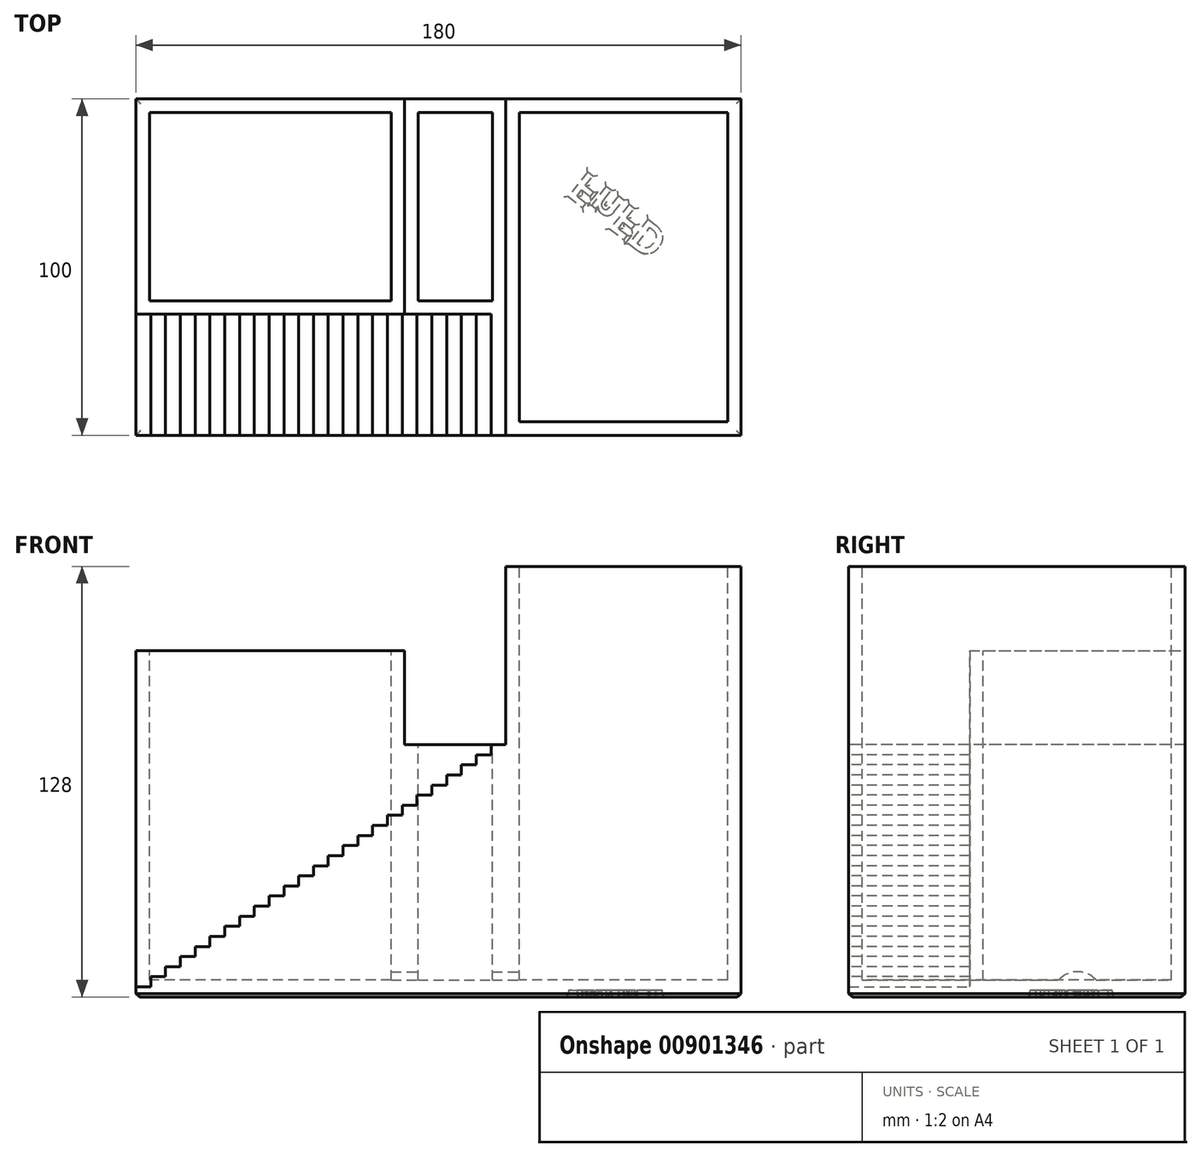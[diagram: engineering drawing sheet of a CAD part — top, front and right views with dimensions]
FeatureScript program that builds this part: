
annotation { "Feature Type Name" : "Feature", "Feature Type Description" : "" }
export const myFeature = defineFeature(function(context is Context, id is Id, definition is map)
    precondition{}
    {
        {
            var Q0;
            Q0=qCreatedBy(makeId("Top.planeOp"),FACE);
            var sketch = newSketch(context, id + "F0", { "sketchPlane" : qUnion([Q0])});
            skLineSegment(sketch, "E0.bottom", {"start": v(-90, -50) * mm, "end": v(90, -50) * mm});
            skLineSegment(sketch, "E0.top", {"start": v(-90, 50) * mm, "end": v(90, 50) * mm});
            skLineSegment(sketch, "E0.left", {"start": v(-90, -50) * mm, "end": v(-90, 50) * mm});
            skLineSegment(sketch, "E0.right", {"start": v(90, -50) * mm, "end": v(90, 50) * mm});
            skPoint(sketch, "E0.middle", {"position": v(0, 0) * mm});
            skSolve(sketch);
        }
        {
            var Q0;
            Q0=makeQuery(id+"F0.imprint","IMPRINT",FACE,{"disambiguationData":[TD([[makeQuery(id+"F0.imprint","IMPRINT",EDGE,{"derivedFrom":sQuery(id+"F0.wireOp",EDGE,"E0.bottom")}),1.0]])]});
            extrude(context, id + "F1", {"entities" : qUnion([Q0]), "depth" : 128 * mm, "offsetDistance" : 25 * mm});
        }
        {
            var Q0;
            Q0=makeQuery(id+"F1.opExtrude","SWEPT_FACE",FACE,{"disambiguationData":[OSD([sQuery(id+"F0.wireOp",EDGE,"E0.bottom")])]});
            var sketch = newSketch(context, id + "F2", { "sketchPlane" : qUnion([Q0])});
            skLineSegment(sketch, "E1.bottom", {"start": v(-90, 128) * mm, "end": v(20, 128) * mm});
            skLineSegment(sketch, "E1.top", {"start": v(-90, 75) * mm, "end": v(20, 75) * mm});
            skLineSegment(sketch, "E1.left", {"start": v(-90, 128) * mm, "end": v(-90, 75) * mm});
            skLineSegment(sketch, "E1.right", {"start": v(20, 128) * mm, "end": v(20, 75) * mm});
            skLineSegment(sketch, "E2", {"start": v(-90, 0) * mm, "end": v(20, 75) * mm, "construction": true});
            skLineSegment(sketch, "E3", {"start": v(-90, 0) * mm, "end": v(-90, 3) * mm});
            skLineSegment(sketch, "E4", {"start": v(-90, 3) * mm, "end": v(-85.6, 3) * mm});
            skLineSegment(sketch, "E5", {"start": v(-85.6, 3) * mm, "end": v(-85.6, 6) * mm});
            skLineSegment(sketch, "E6", {"start": v(-85.6, 6) * mm, "end": v(-81.2, 6) * mm});
            skLineSegment(sketch, "E7", {"start": v(-81.2, 6) * mm, "end": v(-81.2, 9) * mm});
            skLineSegment(sketch, "E8", {"start": v(-81.2, 9) * mm, "end": v(-76.8, 9) * mm});
            skLineSegment(sketch, "E9", {"start": v(-76.8, 9) * mm, "end": v(-76.8, 12) * mm});
            skLineSegment(sketch, "E10", {"start": v(-76.8, 12) * mm, "end": v(-72.4, 12) * mm});
            skLineSegment(sketch, "E11", {"start": v(-72.4, 12) * mm, "end": v(-72.4, 15) * mm});
            skLineSegment(sketch, "E12", {"start": v(-72.4, 15) * mm, "end": v(-68, 15) * mm});
            skLineSegment(sketch, "E13", {"start": v(-68, 15) * mm, "end": v(-68, 18) * mm});
            skLineSegment(sketch, "E14", {"start": v(-68, 18) * mm, "end": v(-63.6, 18) * mm});
            skLineSegment(sketch, "E15", {"start": v(-63.6, 18) * mm, "end": v(-63.6, 21) * mm});
            skLineSegment(sketch, "E16", {"start": v(-63.6, 21) * mm, "end": v(-59.2, 21) * mm});
            skLineSegment(sketch, "E17", {"start": v(-59.2, 21) * mm, "end": v(-59.2, 24) * mm});
            skLineSegment(sketch, "E18", {"start": v(-59.2, 24) * mm, "end": v(-54.8, 24) * mm});
            skLineSegment(sketch, "E19", {"start": v(-54.8, 24) * mm, "end": v(-54.8, 27) * mm});
            skLineSegment(sketch, "E20", {"start": v(-54.8, 27) * mm, "end": v(-50.4, 27) * mm});
            skLineSegment(sketch, "E21", {"start": v(-50.4, 27) * mm, "end": v(-50.4, 30) * mm});
            skLineSegment(sketch, "E22", {"start": v(-50.4, 30) * mm, "end": v(-46, 30) * mm});
            skLineSegment(sketch, "E23", {"start": v(-46, 30) * mm, "end": v(-46, 33) * mm});
            skLineSegment(sketch, "E24", {"start": v(-46, 33) * mm, "end": v(-41.6, 33) * mm});
            skLineSegment(sketch, "E25", {"start": v(-41.6, 33) * mm, "end": v(-41.6, 36) * mm});
            skLineSegment(sketch, "E26", {"start": v(-41.6, 36) * mm, "end": v(-37.2, 36) * mm});
            skLineSegment(sketch, "E27", {"start": v(-37.2, 36) * mm, "end": v(-37.2, 39) * mm});
            skLineSegment(sketch, "E28", {"start": v(-37.2, 39) * mm, "end": v(-32.8, 39) * mm});
            skLineSegment(sketch, "E29", {"start": v(-32.8, 39) * mm, "end": v(-32.8, 42) * mm});
            skLineSegment(sketch, "E30", {"start": v(-32.8, 42) * mm, "end": v(-28.4, 42) * mm});
            skLineSegment(sketch, "E31", {"start": v(-28.4, 42) * mm, "end": v(-28.4, 45) * mm});
            skLineSegment(sketch, "E32", {"start": v(-28.4, 45) * mm, "end": v(-24, 45) * mm});
            skLineSegment(sketch, "E33", {"start": v(-24, 45) * mm, "end": v(-24, 48) * mm});
            skLineSegment(sketch, "E34", {"start": v(-24, 48) * mm, "end": v(-19.6, 48) * mm});
            skLineSegment(sketch, "E35", {"start": v(-19.6, 48) * mm, "end": v(-19.6, 51) * mm});
            skLineSegment(sketch, "E36", {"start": v(-19.6, 51) * mm, "end": v(-15.2, 51) * mm});
            skLineSegment(sketch, "E37", {"start": v(-15.2, 51) * mm, "end": v(-15.2, 54) * mm});
            skLineSegment(sketch, "E38", {"start": v(-15.2, 54) * mm, "end": v(-10.8, 54) * mm});
            skLineSegment(sketch, "E39", {"start": v(-10.8, 54) * mm, "end": v(-10.8, 57) * mm});
            skLineSegment(sketch, "E40", {"start": v(-10.8, 57) * mm, "end": v(-6.4, 57) * mm});
            skLineSegment(sketch, "E41", {"start": v(-6.4, 57) * mm, "end": v(-6.4, 60) * mm});
            skLineSegment(sketch, "E42", {"start": v(-6.4, 60) * mm, "end": v(-2, 60) * mm});
            skLineSegment(sketch, "E43", {"start": v(-2, 60) * mm, "end": v(-2, 63) * mm});
            skLineSegment(sketch, "E44", {"start": v(-2, 63) * mm, "end": v(2.4, 63) * mm});
            skLineSegment(sketch, "E45", {"start": v(2.4, 63) * mm, "end": v(2.4, 63) * mm});
            skLineSegment(sketch, "E46", {"start": v(2.4, 63) * mm, "end": v(2.4, 66) * mm});
            skLineSegment(sketch, "E47", {"start": v(2.4, 66) * mm, "end": v(6.8, 66) * mm});
            skLineSegment(sketch, "E48", {"start": v(6.8, 66) * mm, "end": v(6.8, 69) * mm});
            skLineSegment(sketch, "E49", {"start": v(6.8, 69) * mm, "end": v(11.2, 69) * mm});
            skLineSegment(sketch, "E50", {"start": v(11.2, 69) * mm, "end": v(11.2, 72) * mm});
            skLineSegment(sketch, "E51", {"start": v(11.2, 72) * mm, "end": v(15.6, 72) * mm});
            skLineSegment(sketch, "E52", {"start": v(15.6, 72) * mm, "end": v(15.6, 75) * mm});
            skLineSegment(sketch, "E53", {"start": v(15.6, 75) * mm, "end": v(20, 75) * mm});
            skLineSegment(sketch, "E54", {"start": v(20, 75) * mm, "end": v(20, 78) * mm});
            skLineSegment(sketch, "E55.bottom", {"start": v(20, 75) * mm, "end": v(-10.09, 75) * mm});
            skLineSegment(sketch, "E55.top", {"start": v(20, 128) * mm, "end": v(-10.09, 128) * mm});
            skLineSegment(sketch, "E55.left", {"start": v(20, 75) * mm, "end": v(20, 128) * mm});
            skLineSegment(sketch, "E55.right", {"start": v(-10.09, 75) * mm, "end": v(-10.09, 128) * mm});
            skSolve(sketch);
        }
        {
            var Q0;
            {var subQ4=sQuery(id+"F2.wireOp",EDGE,"E55.right");Q0=makeQuery(id+"F2.imprint","IMPRINT",FACE,{"disambiguationData":[TD([[makeQuery(id+"F2.imprint","IMPRINT",EDGE,{"derivedFrom":subQ4}),-1.0]])]});}
            extrude(context, id + "F3", {"entities" : qUnion([Q0]), "operationType" : NewBodyOperationType.REMOVE, "endBound" : BoundingType.UP_TO_NEXT, "oppositeDirection" : true, "depth" : 25 * mm, "offsetDistance" : 25 * mm});
        }
        {
            var Q0;
            {var subQ5=sQuery(id+"F2.wireOp",EDGE,"E4");Q0=makeQuery(id+"F2.imprint","IMPRINT",FACE,{"disambiguationData":[TD([[makeQuery(id+"F2.imprint","IMPRINT",EDGE,{"derivedFrom":subQ5}),1.0]])]});}
            var Q1;
            {var subQ0=sQuery(id+"F2.wireOp",EDGE,"E1.left");Q1=makeQuery(id+"F2.imprint","IMPRINT",FACE,{"disambiguationData":[TD([[makeQuery(id+"F2.imprint","IMPRINT",EDGE,{"derivedFrom":subQ0}),1.0]])]});}
            extrude(context, id + "F4", {"entities" : qUnion([Q0, Q1]), "operationType" : NewBodyOperationType.REMOVE, "oppositeDirection" : true, "depth" : 36 * mm, "offsetDistance" : 25 * mm});
        }
        {
            var Q0;
            {var subQ0=sQuery(id+"F0.wireOp",EDGE,"E0.bottom");var subQ1=sQuery(id+"F0.wireOp",EDGE,"E0.top");var subQ2=sQuery(id+"F0.wireOp",EDGE,"E0.left");Q0=makeQuery(id+"F3.boolean.opBoolean","SPLIT",FACE,{"disambiguationData":[TD([makeQuery(id+"F1.opExtrude","SWEPT_FACE",FACE,{"disambiguationData":[OSD([subQ2])]})])],"derivedFrom":makeQuery(id+"F1.opExtrude","CAP_FACE",FACE,{"disambiguationData":[OSD([subQ0,subQ1,subQ2,sQuery(id+"F0.wireOp",EDGE,"E0.right")])],"isStart":false})});}
            extrude(context, id + "F5", {"entities" : qUnion([Q0]), "operationType" : NewBodyOperationType.REMOVE, "oppositeDirection" : true, "depth" : 25 * mm, "offsetDistance" : 25 * mm});
        }
        {
            var Q0;
            Q0=makeQuery(id+"F5.boolean.opBoolean","COPY",FACE,{"derivedFrom":makeQuery(id+"F5.opExtrude","CAP_FACE",FACE,{"disambiguationData":[OSD([sQuery(id+"F0.wireOp",EDGE,"E0.bottom"),sQuery(id+"F0.wireOp",EDGE,"E0.top"),sQuery(id+"F0.wireOp",EDGE,"E0.left"),sQuery(id+"F0.wireOp",EDGE,"E0.right")])],"isStart":false})});
            var sketch = newSketch(context, id + "F6", { "sketchPlane" : qUnion([Q0])});
            skLineSegment(sketch, "E56.0", {"start": v(-86, -10) * mm, "end": v(-14.09, -10) * mm});
            skLineSegment(sketch, "E56.1", {"start": v(-86, -10) * mm, "end": v(-86, 46) * mm});
            skLineSegment(sketch, "E56.2", {"start": v(-86, 46) * mm, "end": v(-14.09, 46) * mm});
            skLineSegment(sketch, "E56.3", {"start": v(-14.09, 46) * mm, "end": v(-14.09, -10) * mm});
            skSolve(sketch);
        }
        {
            var Q0;
            {var subQ0=sQuery(id+"F0.wireOp",EDGE,"E0.bottom");var subQ1=sQuery(id+"F0.wireOp",EDGE,"E0.right");var subQ2=sQuery(id+"F0.wireOp",EDGE,"E0.top");Q0=makeQuery(id+"F3.boolean.opBoolean","SPLIT",FACE,{"disambiguationData":[TD([makeQuery(id+"F1.opExtrude","SWEPT_FACE",FACE,{"disambiguationData":[OSD([subQ1])]})])],"derivedFrom":makeQuery(id+"F1.opExtrude","CAP_FACE",FACE,{"disambiguationData":[OSD([subQ0,subQ2,sQuery(id+"F0.wireOp",EDGE,"E0.left"),subQ1])],"isStart":false})});}
            var sketch = newSketch(context, id + "F7", { "sketchPlane" : qUnion([Q0])});
            skLineSegment(sketch, "E57.0", {"start": v(24, 46) * mm, "end": v(86, 46) * mm});
            skLineSegment(sketch, "E57.1", {"start": v(24, 46) * mm, "end": v(24, -46) * mm});
            skLineSegment(sketch, "E57.2", {"start": v(24, -46) * mm, "end": v(86, -46) * mm});
            skLineSegment(sketch, "E57.3", {"start": v(86, -46) * mm, "end": v(86, 46) * mm});
            skSolve(sketch);
        }
        {
            var Q0;
            Q0=makeQuery(id+"F3.boolean.opBoolean","COPY",FACE,{"derivedFrom":makeQuery(id+"F3.opExtrude","SWEPT_FACE",FACE,{"disambiguationData":[OSD([sQuery(id+"F2.wireOp",EDGE,"E1.top")])]})});
            var sketch = newSketch(context, id + "F8", { "sketchPlane" : qUnion([Q0])});
            skLineSegment(sketch, "E58.bottom", {"start": v(20, 50) * mm, "end": v(-10.09, 50) * mm, "construction": true});
            skLineSegment(sketch, "E58.top", {"start": v(20, -14) * mm, "end": v(-10.09, -14) * mm, "construction": true});
            skLineSegment(sketch, "E58.left", {"start": v(20, 50) * mm, "end": v(20, -14) * mm, "construction": true});
            skLineSegment(sketch, "E58.right", {"start": v(-10.09, 50) * mm, "end": v(-10.09, -14) * mm, "construction": true});
            skPoint(sketch, "E58.middle", {"position": v(4.96, 18) * mm});
            skPoint(sketch, "E58.middle.positionSnap0", {"position": v(4.96, 50) * mm});
            skPoint(sketch, "E58.middle.positionSnap1", {"position": v(-10.09, 18) * mm});
            skPoint(sketch, "E58.centerSnap0", {"position": v(4.96, 50) * mm});
            skPoint(sketch, "E58.centerSnap1", {"position": v(-10.09, 18) * mm});
            skLineSegment(sketch, "E59.0", {"start": v(16, -10) * mm, "end": v(-6.09, -10) * mm});
            skLineSegment(sketch, "E59.1", {"start": v(16, 46) * mm, "end": v(16, -10) * mm});
            skLineSegment(sketch, "E59.2", {"start": v(16, 46) * mm, "end": v(-6.09, 46) * mm});
            skLineSegment(sketch, "E59.3", {"start": v(-6.09, 46) * mm, "end": v(-6.09, -10) * mm});
            skSolve(sketch);
        }
        {
            var Q0;
            Q0=makeQuery(id+"F8.imprint","IMPRINT",FACE,{"disambiguationData":[TD([[makeQuery(id+"F8.imprint","IMPRINT",EDGE,{"derivedFrom":sQuery(id+"F8.wireOp",EDGE,"E59.0")}),-1.0]])]});
            var Q1;
            Q1=makeQuery(id+"F7.imprint","IMPRINT",FACE,{"disambiguationData":[TD([[makeQuery(id+"F7.imprint","IMPRINT",EDGE,{"derivedFrom":sQuery(id+"F7.wireOp",EDGE,"E57.0")}),-1.0]])]});
            var Q2;
            Q2=makeQuery(id+"F6.imprint","IMPRINT",FACE,{"disambiguationData":[TD([[makeQuery(id+"F6.imprint","IMPRINT",EDGE,{"derivedFrom":sQuery(id+"F6.wireOp",EDGE,"E56.0")}),1.0]])]});
            extrude(context, id + "F9", {"entities" : qUnion([Q0, Q1, Q2]), "operationType" : NewBodyOperationType.REMOVE, "endBound" : BoundingType.UP_TO_NEXT, "oppositeDirection" : true, "depth" : 25 * mm, "offsetDistance" : 25 * mm});
        }
        {
            var Q0;
            Q0=makeQuery(id+"F9.boolean.opBoolean","COPY",FACE,{"derivedFrom":makeQuery(id+"F9.opExtrude","SWEPT_FACE",FACE,{"disambiguationData":[OSD([sQuery(id+"F8.wireOp",EDGE,"E59.3")])]})});
            var sketch = newSketch(context, id + "F10", { "sketchPlane" : qUnion([Q0])});
            skArc(sketch, "E60", {"start": v(25.5, 0) * mm, "mid": v(18, 7.5) * mm, "end": v(10.5, 0) * mm});
            skSolve(sketch);
        }
        {
            var Q0;
            {var subQ0=sQuery(id+"F10.wireOp",EDGE,"E60");Q0=makeQuery(id+"F10.imprint","IMPRINT",FACE,{"disambiguationData":[TD([[makeQuery(id+"F10.imprint","IMPRINT",EDGE,{"derivedFrom":subQ0}),1.0]])]});}
            extrude(context, id + "F11", {"entities" : qUnion([Q0]), "operationType" : NewBodyOperationType.REMOVE, "endBound" : BoundingType.SYMMETRIC, "oppositeDirection" : true, "depth" : 70 * mm, "offsetDistance" : 25 * mm});
        }
        {
            var Q0;
            Q0=makeQuery(id+"F0.imprint","IMPRINT",FACE,{"disambiguationData":[TD([[makeQuery(id+"F0.imprint","IMPRINT",EDGE,{"derivedFrom":sQuery(id+"F0.wireOp",EDGE,"E0.bottom")}),1.0]])]});
            extrude(context, id + "F12", {"entities" : qUnion([Q0]), "operationType" : NewBodyOperationType.ADD, "depth" : 5 * mm, "offsetDistance" : 25 * mm});
        }
        {
            var Q0;
            {var subQ0=sQuery(id+"F0.wireOp",EDGE,"E0.right");var subQ1=sQuery(id+"F0.wireOp",EDGE,"E0.left");var subQ2=sQuery(id+"F0.wireOp",EDGE,"E0.top");var subQ3=sQuery(id+"F0.wireOp",EDGE,"E0.bottom");Q0=makeQuery(id+"F12.boolean.opBoolean","MERGE",FACE,{"derivedFrom":[makeQuery(id+"F1.opExtrude","CAP_FACE",FACE,{"disambiguationData":[OSD([subQ3,subQ2,subQ1,subQ0])],"isStart":true}),makeQuery(id+"F12.opExtrude","CAP_FACE",FACE,{"disambiguationData":[OSD([subQ3,subQ2,subQ1,subQ0])],"isStart":true})]});}
            chamfer(context, id + "F13", {"entities" : qUnion([Q0]), "width" : 1 * mm, "tangentPropagation" : true});
        }
        {
            var Q0;
            {var subQ0=sQuery(id+"F0.wireOp",EDGE,"E0.right");var subQ1=sQuery(id+"F0.wireOp",EDGE,"E0.left");var subQ2=sQuery(id+"F0.wireOp",EDGE,"E0.top");var subQ3=sQuery(id+"F0.wireOp",EDGE,"E0.bottom");Q0=makeQuery(id+"F12.boolean.opBoolean","MERGE",FACE,{"derivedFrom":[makeQuery(id+"F1.opExtrude","CAP_FACE",FACE,{"disambiguationData":[OSD([subQ3,subQ2,subQ1,subQ0])],"isStart":true}),makeQuery(id+"F12.opExtrude","CAP_FACE",FACE,{"disambiguationData":[OSD([subQ3,subQ2,subQ1,subQ0])],"isStart":true})]});}
            var sketch = newSketch(context, id + "F14", { "sketchPlane" : qUnion([Q0])});
            skText(sketch, "E61", { "text": "FnFD", "fontName": "OpenSans-Bold.ttf"});
            const initialGuessF14  = {"E61": [0.04341, -0.029, 0.7879, 0.6158, 0.00935]};
            skSetInitialGuess(sketch, initialGuessF14);
            skSolve(sketch);
        }
        {
            var Q0;
            Q0 = qSketchRegion(id + "F14", true);
            extrude(context, id + "F15", {"entities" : qUnion([Q0]), "operationType" : NewBodyOperationType.REMOVE, "oppositeDirection" : true, "depth" : 2 * mm, "offsetDistance" : 25 * mm});
        }
        {
            var Q0;
            Q0=makeQuery(id+"F15.boolean.opBoolean","COPY",EDGE,{"derivedFrom":makeQuery(id+"F15.opExtrude","CAP_EDGE",EDGE,{"disambiguationData":[OSD([sQuery(id+"F14.wireOp",EDGE,"E61.sketch_text.stroke-5")])],"isStart":true})});
            var Q1;
            Q1=makeQuery(id+"F15.boolean.opBoolean","COPY",EDGE,{"derivedFrom":makeQuery(id+"F15.opExtrude","CAP_EDGE",EDGE,{"disambiguationData":[OSD([sQuery(id+"F14.wireOp",EDGE,"E61.sketch_text.stroke-4")])],"isStart":true})});
            var Q2;
            Q2=makeQuery(id+"F15.boolean.opBoolean","COPY",EDGE,{"derivedFrom":makeQuery(id+"F15.opExtrude","CAP_EDGE",EDGE,{"disambiguationData":[OSD([sQuery(id+"F14.wireOp",EDGE,"E61.sketch_text.stroke-3")])],"isStart":true})});
            var Q3;
            Q3=makeQuery(id+"F15.boolean.opBoolean","COPY",EDGE,{"derivedFrom":makeQuery(id+"F15.opExtrude","CAP_EDGE",EDGE,{"disambiguationData":[OSD([sQuery(id+"F14.wireOp",EDGE,"E61.sketch_text.stroke-2")])],"isStart":true})});
            var Q4;
            Q4=makeQuery(id+"F15.boolean.opBoolean","COPY",EDGE,{"derivedFrom":makeQuery(id+"F15.opExtrude","CAP_EDGE",EDGE,{"disambiguationData":[OSD([sQuery(id+"F14.wireOp",EDGE,"E61.sketch_text.stroke-1")])],"isStart":true})});
            var Q5;
            Q5=makeQuery(id+"F15.boolean.opBoolean","COPY",EDGE,{"derivedFrom":makeQuery(id+"F15.opExtrude","CAP_EDGE",EDGE,{"disambiguationData":[OSD([sQuery(id+"F14.wireOp",EDGE,"E61.sketch_text.stroke-0")])],"isStart":true})});
            var Q6;
            {var subQ0=sQuery(id+"F0.wireOp",EDGE,"E0.bottom");var subQ1=sQuery(id+"F0.wireOp",EDGE,"E0.top");var subQ2=sQuery(id+"F0.wireOp",EDGE,"E0.left");var subQ3=sQuery(id+"F0.wireOp",EDGE,"E0.right");Q6=makeQuery(id+"F15.boolean.opBoolean","SPLIT",FACE,{"disambiguationData":[TD([makeQuery(id+"F13.opChamfer","BLEND_FACE",FACE,{"disambiguationData":[OSD([subQ0])]})])],"derivedFrom":makeQuery(id+"F12.boolean.opBoolean","MERGE",FACE,{"derivedFrom":[makeQuery(id+"F1.opExtrude","CAP_FACE",FACE,{"disambiguationData":[OSD([subQ0,subQ1,subQ2,subQ3])],"isStart":true}),makeQuery(id+"F12.opExtrude","CAP_FACE",FACE,{"disambiguationData":[OSD([subQ0,subQ1,subQ2,subQ3])],"isStart":true})]})});}
            var Q7;
            Q7=makeQuery(id+"F15.boolean.opBoolean","COPY",EDGE,{"derivedFrom":makeQuery(id+"F15.opExtrude","CAP_EDGE",EDGE,{"disambiguationData":[OSD([sQuery(id+"F14.wireOp",EDGE,"E61.sketch_text.stroke-8")])],"isStart":true})});
            fillet(context, id + "F16", {"entities" : qUnion([Q0, Q1, Q2, Q3, Q4, Q5, Q6, Q7]), "radius" : 1 * mm, "tangentPropagation" : true, "allowEdgeOverflow" : false});
        }
        {
            var Q0;
            {var subQ1=sQuery(id+"F0.wireOp",EDGE,"E0.left");var subQ2=sQuery(id+"F0.wireOp",EDGE,"E0.bottom");Q0=makeQuery(id+"F12.boolean.opBoolean","SPLIT",FACE,{"disambiguationData":[TD([makeQuery(id+"F1.opExtrude","SWEPT_FACE",FACE,{"disambiguationData":[OSD([subQ2])]})])],"derivedFrom":makeQuery(id+"F12.opExtrude","CAP_FACE",FACE,{"disambiguationData":[OSD([subQ2,sQuery(id+"F0.wireOp",EDGE,"E0.top"),subQ1,sQuery(id+"F0.wireOp",EDGE,"E0.right")])],"isStart":false})});}
            extrude(context, id + "F17", {"entities" : qUnion([Q0]), "operationType" : NewBodyOperationType.REMOVE, "oppositeDirection" : true, "depth" : 2 * mm, "offsetDistance" : 25 * mm});
        }
    });
